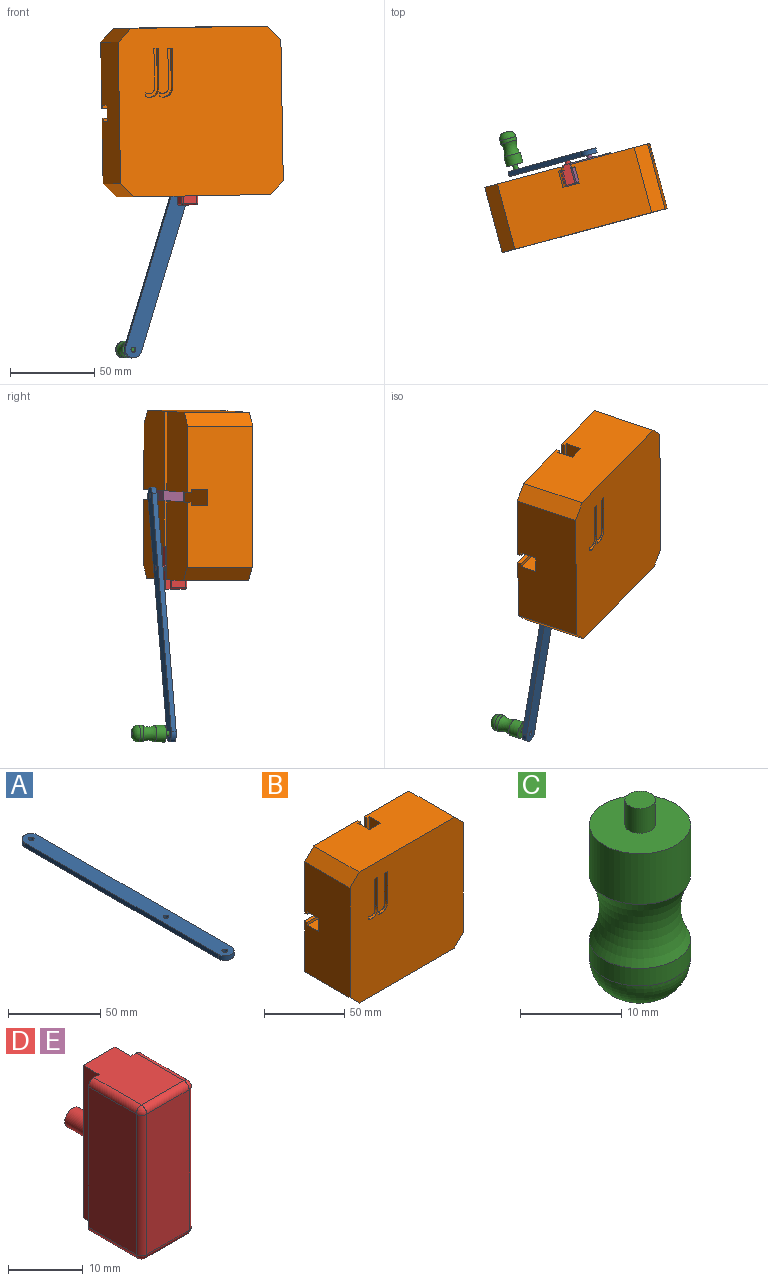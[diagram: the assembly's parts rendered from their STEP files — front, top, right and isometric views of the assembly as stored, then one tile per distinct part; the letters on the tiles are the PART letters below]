
ASSEMBLY  parts=5 mates=7
PART A: 9 faces, bbox 10x158x3 mm
  f0: cylinder r=5mm len=10mm, axis (0,0,-1), area 47.1mm2, adj f1,f6,f7,f8
  f1: plane 148x3mm, normal (-1,0,0), area 444mm2, adj f0,f2,f7,f8
  f2: cylinder r=5mm len=10mm, axis (0,0,-1), area 47.1mm2, adj f1,f6,f7,f8
  f3: cylinder r=1.5mm len=3mm, axis (0,0,-1), area 28.3mm2, adj f7,f8
  f4: cylinder r=1.5mm len=3mm, axis (0,0,-1), area 28.3mm2, adj f7,f8
  f5: cylinder r=1.5mm len=3mm, axis (0,0,-1), area 28.3mm2, adj f7,f8
  f6: plane 148x3mm, normal (1,0,0), area 444mm2, adj f0,f2,f7,f8
  f7: plane 158x10mm, normal (0,0,1), area 1537.3mm2, adj f0,f1,f2,f3,f4,f5,f6
  f8: plane 158x10mm, normal (0,0,-1), area 1537.3mm2, adj f0,f1,f2,f3,f4,f5,f6
PART B: 60 faces, bbox 100x40x100 mm
  f0: plane 100x100mm, normal (0,-1,0), area 9701.5mm2, adj f13,f14,f15,f16,f34,f35,f36,f37
  f1: plane 46.91x46.77mm, normal (0,1,0), area 2162.2mm2, adj f3,f14,f15,f27,f35
  f2: plane 47.09x46.77mm, normal (0,1,0), area 2170.2mm2, adj f11,f14,f16,f29,f34
  f3: plane 46.77x2mm, normal (1,0,0), area 93.5mm2, adj f1,f4,f14,f27
  f4: plane 46.77x1.91mm, normal (0,-1,0), area 89.5mm2, adj f3,f5,f14,f27
  f5: plane 46.77x10mm, normal (1,0,0), area 447.5mm2, adj f4,f14,f20,f23,f24,f27
  f6: plane 47.23x10mm, normal (1,0,0), area 453.4mm2, adj f7,f13,f19,f25,f26,f28
  f7: plane 45.3x10mm, normal (0,1,0), area 453mm2, adj f6,f9,f13,f25
  f8: plane 46.77x10mm, normal (-1,0,0), area 447.5mm2, adj f10,f14,f20,f24,f29,f30
  f9: plane 47.23x10mm, normal (-1,0,0), area 453.4mm2, adj f7,f13,f21,f25,f32,f33
  f10: plane 46.77x2.09mm, normal (0,-1,0), area 97.6mm2, adj f8,f11,f14,f29
  f11: plane 46.77x2mm, normal (-1,0,0), area 93.5mm2, adj f2,f10,f14,f29
  f12: plane 47.23x46.91mm, normal (0,1,0), area 2183.7mm2, adj f13,f15,f18,f28,f36
  f13: plane 84x40mm, normal (0,0,1), area 3248mm2, adj f0,f6,f7,f9,f12,f17,f18,f19
  f14: plane 84x40mm, normal (0,0,-1), area 3248mm2, adj f0,f1,f2,f3,f4,f5,f8,f10
  f15: plane 84x40mm, normal (-1,0,0), area 3246.5mm2, adj f0,f1,f12,f23,f24,f25,f26,f27
  f16: plane 84x40mm, normal (1,0,0), area 3246.5mm2, adj f0,f2,f17,f24,f25,f29,f30,f31
  f17: plane 47.23x47.09mm, normal (0,1,0), area 2191.8mm2, adj f13,f16,f22,f33,f37
  f18: plane 47.23x2mm, normal (1,0,0), area 94.5mm2, adj f12,f13,f19,f28
  f19: plane 47.23x1.91mm, normal (0,-1,0), area 90.4mm2, adj f6,f13,f18,f28
  f20: plane 44.7x10mm, normal (0,1,0), area 447mm2, adj f5,f8,f14,f24
  f21: plane 47.23x2.09mm, normal (0,-1,0), area 98.5mm2, adj f9,f13,f22,f33
  f22: plane 47.23x2mm, normal (-1,0,0), area 94.5mm2, adj f13,f17,f21,f33
  f23: plane 45x2.07mm, normal (0,-1,0), area 93mm2, adj f5,f15,f24,f27
  f24: plane 100x10mm, normal (0,0,1), area 902.5mm2, adj f5,f8,f15,f16,f20,f23,f30,f31
  f25: plane 100x10mm, normal (0,0,-1), area 902.5mm2, adj f6,f7,f9,f15,f16,f26,f31,f32
  f26: plane 45x1.93mm, normal (0,-1,0), area 87mm2, adj f6,f15,f25,f28
  f27: plane 46.91x2.25mm, normal (0,0,1), area 104.9mm2, adj f1,f3,f4,f5,f15,f23
  f28: plane 46.91x2.25mm, normal (0,0,-1), area 104.9mm2, adj f6,f12,f15,f18,f19,f26
  f29: plane 47.09x2.25mm, normal (0,0,1), area 105.2mm2, adj f2,f8,f10,f11,f16,f30
  f30: plane 45x2.07mm, normal (0,-1,0), area 93mm2, adj f8,f16,f24,f29
  f31: plane 100x10mm, normal (0,1,0), area 1000mm2, adj f15,f16,f24,f25
  f32: plane 45x1.93mm, normal (0,-1,0), area 87mm2, adj f9,f16,f25,f33
  f33: plane 47.09x2.25mm, normal (0,0,-1), area 105.2mm2, adj f9,f16,f17,f21,f22,f32
  f34: plane 40x8mm, normal (0.71,0,-0.71), area 452.5mm2, adj f0,f2,f14,f16
  f35: plane 40x8mm, normal (-0.71,0,-0.71), area 452.5mm2, adj f0,f1,f14,f15
  f36: plane 40x8mm, normal (-0.71,0,0.71), area 452.5mm2, adj f0,f12,f13,f15
  f37: plane 40x8mm, normal (0.71,0,0.71), area 452.5mm2, adj f0,f13,f16,f17
  f38: extruded ~3.5x2.31mm, area 8.3mm2, adj f0,f39,f47,f48
  f39: extruded ~4.32x3.5mm, area 16.6mm2, adj f0,f38,f40,f48
  f40: extruded ~4.6x3.5mm, area 17.4mm2, adj f0,f39,f41,f48
  f41: plane 22.64x3.5mm, normal (-1,0,0), area 79.2mm2, adj f0,f40,f42,f48
  f42: plane 3.5x2.66mm, normal (0,0,-1), area 9.3mm2, adj f0,f41,f43,f48
  f43: plane 22.86x3.5mm, normal (1,0,0), area 80mm2, adj f0,f42,f44,f48
  f44: extruded ~3.5x2.7mm, area 10.1mm2, adj f0,f43,f45,f48
  f45: extruded ~3.5x2.36mm, area 9.2mm2, adj f0,f44,f46,f48
  f46: extruded ~3.5x2.31mm, area 8.2mm2, adj f0,f45,f47,f48
  f47: plane 3.5x2.27mm, normal (1,0,0), area 7.9mm2, adj f0,f38,f46,f48
  f48: plane 28.87x8.13mm, normal (0,-1,0), area 85.2mm2, adj f38,f39,f40,f41,f42,f43,f44,f45
  f49: extruded ~3.5x2.31mm, area 8.3mm2, adj f0,f50,f58,f59
  f50: extruded ~4.32x3.5mm, area 16.6mm2, adj f0,f49,f51,f59
  f51: extruded ~4.6x3.5mm, area 17.4mm2, adj f0,f50,f52,f59
  f52: plane 22.64x3.5mm, normal (-1,0,0), area 79.2mm2, adj f0,f51,f53,f59
  f53: plane 3.5x2.66mm, normal (0,0,-1), area 9.3mm2, adj f0,f52,f54,f59
  f54: plane 22.86x3.5mm, normal (1,0,0), area 80mm2, adj f0,f53,f55,f59
  f55: extruded ~3.5x2.7mm, area 10.1mm2, adj f0,f54,f56,f59
  f56: extruded ~3.5x2.36mm, area 9.2mm2, adj f0,f55,f57,f59
  f57: extruded ~3.5x2.31mm, area 8.2mm2, adj f0,f56,f58,f59
  f58: plane 3.5x2.27mm, normal (1,0,0), area 7.9mm2, adj f0,f49,f57,f59
  f59: plane 28.87x8.13mm, normal (0,-1,0), area 85.2mm2, adj f49,f50,f51,f52,f53,f54,f55,f56
PART C: 8 faces, bbox 13.7x13.7x23 mm
  f0: plane 2x2mm, normal (0,0,-1), area 3.1mm2, adj f1
  f1: torus R=1mm, axis (0,0,-1), area 140mm2, adj f0,f2
  f2: cylinder r=5mm len=10mm, axis (0,0,-1), area 66.8mm2, adj f1,f3
  f3: torus R=12mm, axis (0,0,-1), area 220.3mm2, adj f2,f4
  f4: cylinder r=5mm len=10mm, axis (0,0,-1), area 192.5mm2, adj f3,f5
  f5: plane 10x10mm, normal (0,0,1), area 71.5mm2, adj f4,f6
  f6: cylinder r=1.5mm len=3mm, axis (0,0,-1), area 28.3mm2, adj f5,f7
  f7: plane 3x3mm, normal (0,0,1), area 7.1mm2, adj f6
PART D: 24 faces, bbox 10x18x25 mm
  f0: plane 25x3mm, normal (-1,0,0), area 75mm2, adj f1,f7,f8,f9
  f1: plane 25x2mm, normal (0,1,0), area 49.6mm2, adj f0,f2,f8,f9,f17,f20
  f2: plane 23x9mm, normal (-1,0,0), area 207mm2, adj f1,f17,f20,f23
  f3: plane 23x8mm, normal (0,-1,0), area 184mm2, adj f13,f18,f19,f23
  f4: plane 23x9mm, normal (1,0,0), area 207mm2, adj f5,f12,f13,f14
  f5: plane 25x2mm, normal (0,1,0), area 49.6mm2, adj f4,f6,f8,f9,f12,f14
  f6: plane 25x3mm, normal (1,0,0), area 75mm2, adj f5,f7,f8,f9
  f7: plane 25x6mm, normal (0,1,0), area 142.9mm2, adj f0,f6,f8,f9,f10
  f8: plane 12x8mm, normal (0,0,1), area 90mm2, adj f0,f1,f5,f6,f7,f12,f17,f18
  f9: plane 12x8mm, normal (0,0,-1), area 90mm2, adj f0,f1,f5,f6,f7,f14,f19,f20
  f10: cylinder r=1.5mm len=5mm, axis (0,-1,0), area 47.1mm2, adj f7,f11
  f11: plane 3x3mm, normal (0,1,0), area 7.1mm2, adj f10
  f12: cylinder r=1mm len=9mm, axis (0,-1,0), area 14.1mm2, adj f4,f5,f8,f15
  f13: cylinder r=1mm len=23mm, axis (0,0,-1), area 36.1mm2, adj f3,f4,f15,f16
  f14: cylinder r=1mm len=9mm, axis (0,1,0), area 14.1mm2, adj f4,f5,f9,f16
  f15: sphere r=1mm, area 1.6mm2, adj f12,f13,f18
  f16: sphere r=1mm, area 1.6mm2, adj f13,f14,f19
  f17: cylinder r=1mm len=9mm, axis (0,1,0), area 14.1mm2, adj f1,f2,f8,f21
  f18: cylinder r=1mm len=8mm, axis (-1,0,0), area 12.6mm2, adj f3,f8,f15,f21
  f19: cylinder r=1mm len=8mm, axis (1,0,0), area 12.6mm2, adj f3,f9,f16,f22
  f20: cylinder r=1mm len=9mm, axis (0,-1,0), area 14.1mm2, adj f1,f2,f9,f22
  f21: sphere r=1mm, area 1.6mm2, adj f17,f18,f23
  f22: sphere r=1mm, area 1.6mm2, adj f19,f20,f23
  f23: cylinder r=1mm len=23mm, axis (0,0,1), area 36.1mm2, adj f2,f3,f21,f22
PART E: same geometry as D
PLACE A rot(axis=(-0.96,0.02,0.27),94.4deg) t=(80.14,-27.95,20.25)mm
PLACE B rot(axis=(0.01,-0.07,1),15deg) t=(130.04,-17.43,-7.07)mm fixed
PLACE C rot(axis=(0.2,-0.68,0.71),178.4deg) t=(101.58,45.24,-79.48)mm
PLACE D rot(axis=(0.01,-0.07,1),15deg) t=(118.29,-89.68,-55.83)mm
PLACE E rot(axis=(0.13,-0.98,0.13),92deg) t=(172.99,-75.02,-30.05)mm
MATE fastened A.f0 <-> C.f1  axis (-0.26,0.97,0) through (99.1,-19.76,-141.14)mm
MATE planar E.f2 <-> B.f24  axis (0.02,0,-1) through (144.96,-20.42,-4.84)mm
MATE revolute A.f2 <-> E.f10  axis (-0.26,0.97,0) through (141.64,-8.37,0.16)mm
MATE planar D.f2 <-> B.f5  axis (-0.97,-0.26,-0.02) through (127.11,-25.2,-42.89)mm
MATE revolute A.f7 <-> A.f0  axis (-0.26,0.97,0) through (94.49,-21,-139.65)mm
MATE revolute D.f10 <-> A.f5  axis (-0.26,0.97,0) through (128.7,-11.83,-42.8)mm
MATE planar E.f10 <-> B.f31  axis (0.26,-0.97,0) through (146.3,-25.75,0.16)mm
